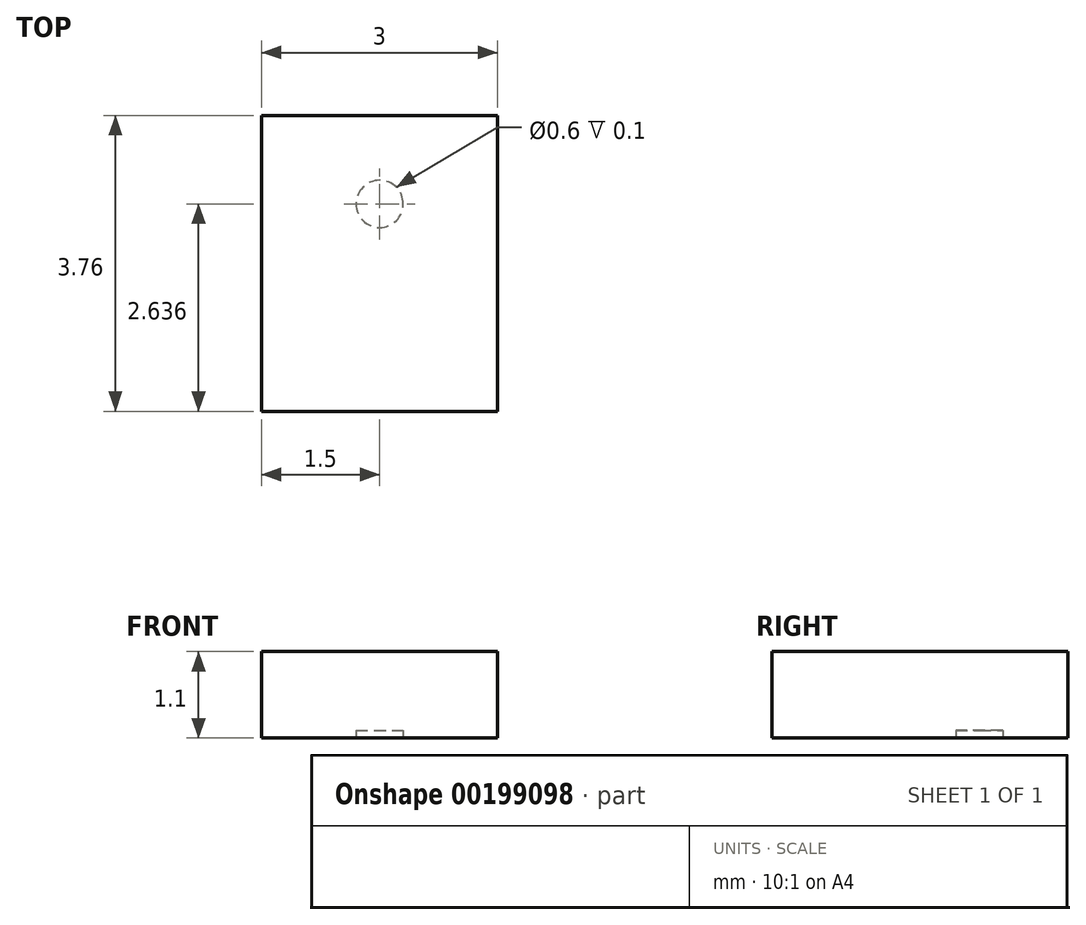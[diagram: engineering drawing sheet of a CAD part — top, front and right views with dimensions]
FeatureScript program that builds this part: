
annotation { "Feature Type Name" : "Feature", "Feature Type Description" : "" }
export const myFeature = defineFeature(function(context is Context, id is Id, definition is map)
    precondition{}
    {
        {
            var Q0;
            Q0=qCreatedBy(makeId("Top.planeOp"),FACE);
            var sketch = newSketch(context, id + "F0", { "sketchPlane" : qUnion([Q0])});
            skLineSegment(sketch, "E0.bottom", {"start": v(1.5, 1.88) * mm, "end": v(-1.5, 1.88) * mm});
            skLineSegment(sketch, "E0.top", {"start": v(1.5, -1.88) * mm, "end": v(-1.5, -1.88) * mm});
            skLineSegment(sketch, "E0.left", {"start": v(1.5, 1.88) * mm, "end": v(1.5, -1.88) * mm});
            skLineSegment(sketch, "E0.right", {"start": v(-1.5, 1.88) * mm, "end": v(-1.5, -1.88) * mm});
            skPoint(sketch, "E0.middle", {"position": v(0, 0) * mm});
            skSolve(sketch);
        }
        {
            var Q0;
            Q0 = qSketchRegion(id + "F0", true);
            extrude(context, id + "F1", {"entities" : qUnion([Q0]), "depth" : 1.1 * mm});
        }
        {
            var Q0;
            Q0=makeQuery(id+"F1.opExtrude","CAP_FACE",FACE,{"disambiguationData":[OSD([sQuery(id+"F0.wireOp",EDGE,"E0.bottom"),sQuery(id+"F0.wireOp",EDGE,"E0.top"),sQuery(id+"F0.wireOp",EDGE,"E0.left"),sQuery(id+"F0.wireOp",EDGE,"E0.right")])],"isStart":true});
            var sketch = newSketch(context, id + "F2", { "sketchPlane" : qUnion([Q0])});
            skCircle(sketch, "E1", {"center": v(0, -0.76) * mm, "radius": 0.3 * mm});
            skSolve(sketch);
        }
        {
            var Q0;
            Q0 = qSketchRegion(id + "F2", true);
            extrude(context, id + "F3", {"entities" : qUnion([Q0]), "operationType" : NewBodyOperationType.REMOVE, "oppositeDirection" : true, "depth" : .1 * mm});
        }
    });
